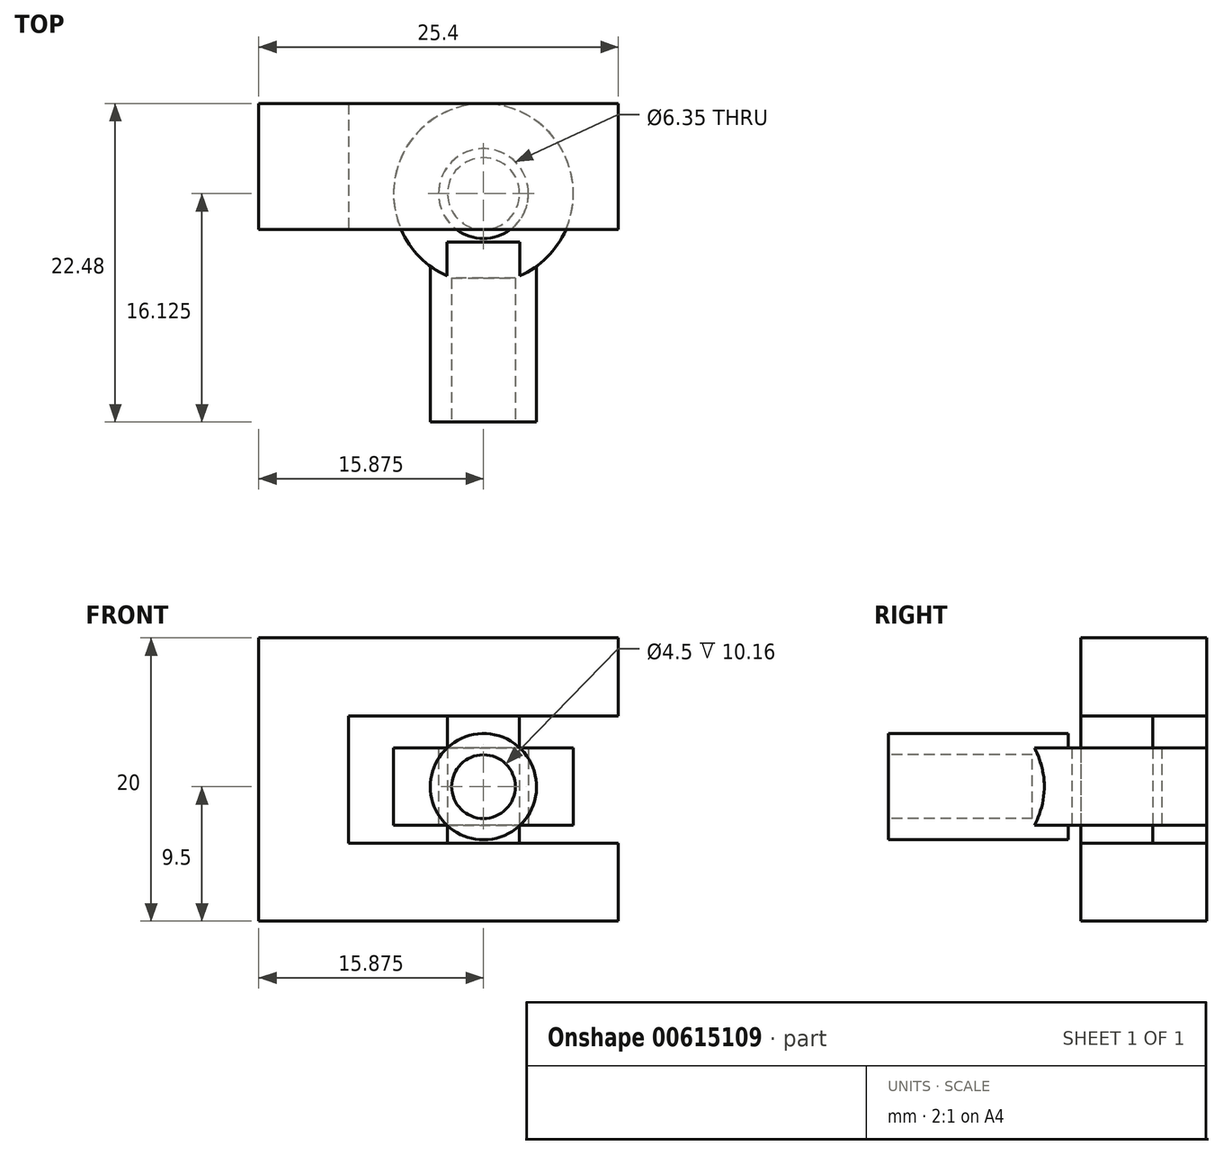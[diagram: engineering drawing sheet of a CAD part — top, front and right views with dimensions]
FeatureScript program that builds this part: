
annotation { "Feature Type Name" : "Feature", "Feature Type Description" : "" }
export const myFeature = defineFeature(function(context is Context, id is Id, definition is map)
    precondition{}
    {
        {
            var Q0;
            Q0=qCreatedBy(makeId("Top.planeOp"),FACE);
            var sketch = newSketch(context, id + "F0", { "sketchPlane" : qUnion([Q0])});
            skLineSegment(sketch, "E0.bottom", {"start": v(-12.7, 4.45) * mm, "end": v(12.7, 4.45) * mm});
            skLineSegment(sketch, "E0.top", {"start": v(-12.7, -4.44) * mm, "end": v(12.7, -4.44) * mm});
            skLineSegment(sketch, "E0.left", {"start": v(-12.7, 4.45) * mm, "end": v(-12.7, -4.44) * mm});
            skLineSegment(sketch, "E0.right", {"start": v(12.7, 4.45) * mm, "end": v(12.7, -4.44) * mm});
            skPoint(sketch, "E0.middle", {"position": v(0, 0) * mm});
            skSolve(sketch);
        }
        {
            var Q0;
            Q0=qSketchRegion(id+"F0",true);
            extrude(context, id + "F1", {"entities" : qUnion([Q0]), "endBound" : BoundingType.SYMMETRIC, "depth" : 20 * mm, "offsetDistance" : 25.4 * mm});
        }
        {
            var Q0;
            Q0=makeQuery(id+"F1.opExtrude","SWEPT_FACE",FACE,{"disambiguationData":[OSD([sQuery(id+"F0.wireOp",EDGE,"E0.top")])]});
            var sketch = newSketch(context, id + "F2", { "sketchPlane" : qUnion([Q0])});
            skLineSegment(sketch, "E1.bottom", {"start": v(-6.35, 4.5) * mm, "end": v(12.7, 4.5) * mm});
            skLineSegment(sketch, "E1.top", {"start": v(-6.35, -4.5) * mm, "end": v(12.7, -4.5) * mm});
            skLineSegment(sketch, "E1.left", {"start": v(-6.35, 4.5) * mm, "end": v(-6.35, -4.5) * mm});
            skLineSegment(sketch, "E1.right", {"start": v(12.7, 4.5) * mm, "end": v(12.7, -4.5) * mm});
            skPoint(sketch, "E1.middle", {"position": v(3.18, 0) * mm});
            skSolve(sketch);
        }
        {
            var Q0;
            Q0=qSketchRegion(id+"F2",true);
            extrude(context, id + "F3", {"entities" : qUnion([Q0]), "operationType" : NewBodyOperationType.REMOVE, "endBound" : BoundingType.THROUGH_ALL, "oppositeDirection" : true, "depth" : 25.4 * mm, "offsetDistance" : 25.4 * mm});
        }
        {
            var Q0;
            Q0=makeQuery(id+"F3.boolean.opBoolean","COPY",FACE,{"derivedFrom":makeQuery(id+"F3.opExtrude","SWEPT_FACE",FACE,{"disambiguationData":[OSD([sQuery(id+"F2.wireOp",EDGE,"E1.top")])]})});
            var sketch = newSketch(context, id + "F4", { "sketchPlane" : qUnion([Q0])});
            skCircle(sketch, "E2", {"center": v(3.17, -1.9) * mm, "radius": 2.54 * mm});
            skSolve(sketch);
        }
        {
            var Q0;
            Q0=qSketchRegion(id+"F4",true);
            extrude(context, id + "F5", {"entities" : qUnion([Q0]), "operationType" : NewBodyOperationType.ADD, "endBound" : BoundingType.UP_TO_NEXT, "depth" : 25.4 * mm, "offsetDistance" : 25.4 * mm});
        }
        {
            var Q0;
            Q0=makeQuery(id+"F3.boolean.opBoolean","COPY",FACE,{"derivedFrom":makeQuery(id+"F3.opExtrude","SWEPT_FACE",FACE,{"disambiguationData":[OSD([sQuery(id+"F2.wireOp",EDGE,"E1.top")])]})});
            cPlane(context, id + "F6", {"entities" : qUnion([Q0]), "cplaneType" : CPlaneType.OFFSET, "offset" : 1.27 * mm, "width" : 152.4 * mm, "height" : 152.4 * mm});
        }
        {
            var Q0;
            Q0=qCreatedBy(id+"F6.planeOp",FACE);
            var sketch = newSketch(context, id + "F7", { "sketchPlane" : qUnion([Q0])});
            skCircle(sketch, "E3.0", {"center": v(3.17, -1.9) * mm, "radius": 2.54 * mm});
            skCircle(sketch, "E4", {"center": v(3.17, -1.9) * mm, "radius": 3.17 * mm});
            skLineSegment(sketch, "E5.0", {"start": v(12.7, 4.45) * mm, "end": v(-6.35, 4.45) * mm});
            skCircle(sketch, "E6", {"center": v(3.17, -1.9) * mm, "radius": 6.35 * mm});
            skSolve(sketch);
        }
        {
            var Q0;
            Q0=qSketchRegion(id+"F7",true);
            extrude(context, id + "F8", {"entities" : qUnion([Q0]), "depth" : 8 * mm - 2.54 * mm, "offsetDistance" : 25.4 * mm});
        }
        {
            var Q0;
            Q0=makeQuery(id+"F1.opExtrude","SWEPT_FACE",FACE,{"disambiguationData":[OSD([sQuery(id+"F0.wireOp",EDGE,"E0.top")])]});
            cPlane(context, id + "F9", {"entities" : qUnion([Q0]), "cplaneType" : CPlaneType.OFFSET, "offset" : 0.89 * mm, "width" : 152.4 * mm, "height" : 152.4 * mm});
        }
        {
            var Q0;
            Q0=qCreatedBy(id+"F9.planeOp",FACE);
            var sketch = newSketch(context, id + "F10", { "sketchPlane" : qUnion([Q0])});
            skLineSegment(sketch, "E7.0.0", {"start": v(9.52, -3.23) * mm, "end": v(-3.18, -3.23) * mm});
            skLineSegment(sketch, "E8.0.0", {"start": v(-3.18, 2.23) * mm, "end": v(9.52, 2.23) * mm});
            skLineSegment(sketch, "E9", {"start": v(3.17, 2.23) * mm, "end": v(3.17, -3.23) * mm, "construction": true});
            skCircle(sketch, "E10", {"center": v(3.17, -0.5) * mm, "radius": 3.75 * mm});
            skSolve(sketch);
        }
        {
            var Q0;
            Q0=qSketchRegion(id+"F10",true);
            extrude(context, id + "F11", {"entities" : qUnion([Q0]), "operationType" : NewBodyOperationType.ADD, "depth" : 12.7 * mm, "offsetDistance" : 25.4 * mm});
        }
        {
            var Q0;
            Q0=makeQuery(id+"F11.opExtrude","CAP_FACE",FACE,{"disambiguationData":[OSD([sQuery(id+"F10.wireOp",EDGE,"E10")])],"isStart":false});
            var sketch = newSketch(context, id + "F12", { "sketchPlane" : qUnion([Q0])});
            skCircle(sketch, "E11.0", {"center": v(3.17, -0.5) * mm, "radius": 3.75 * mm, "construction": true});
            skCircle(sketch, "E12", {"center": v(3.17, -0.5) * mm, "radius": 2.25 * mm});
            skSolve(sketch);
        }
        {
            var Q0;
            Q0=makeQuery(id+"F12.imprint","IMPRINT",FACE,{"disambiguationData":[TD([[makeQuery(id+"F12.imprint","IMPRINT",EDGE,{"derivedFrom":sQuery(id+"F12.wireOp",EDGE,"E12")}),1.0]])]});
            extrude(context, id + "F13", {"entities" : qUnion([Q0]), "operationType" : NewBodyOperationType.REMOVE, "oppositeDirection" : true, "depth" : 10.16 * mm, "offsetDistance" : 25.4 * mm});
        }
    });
